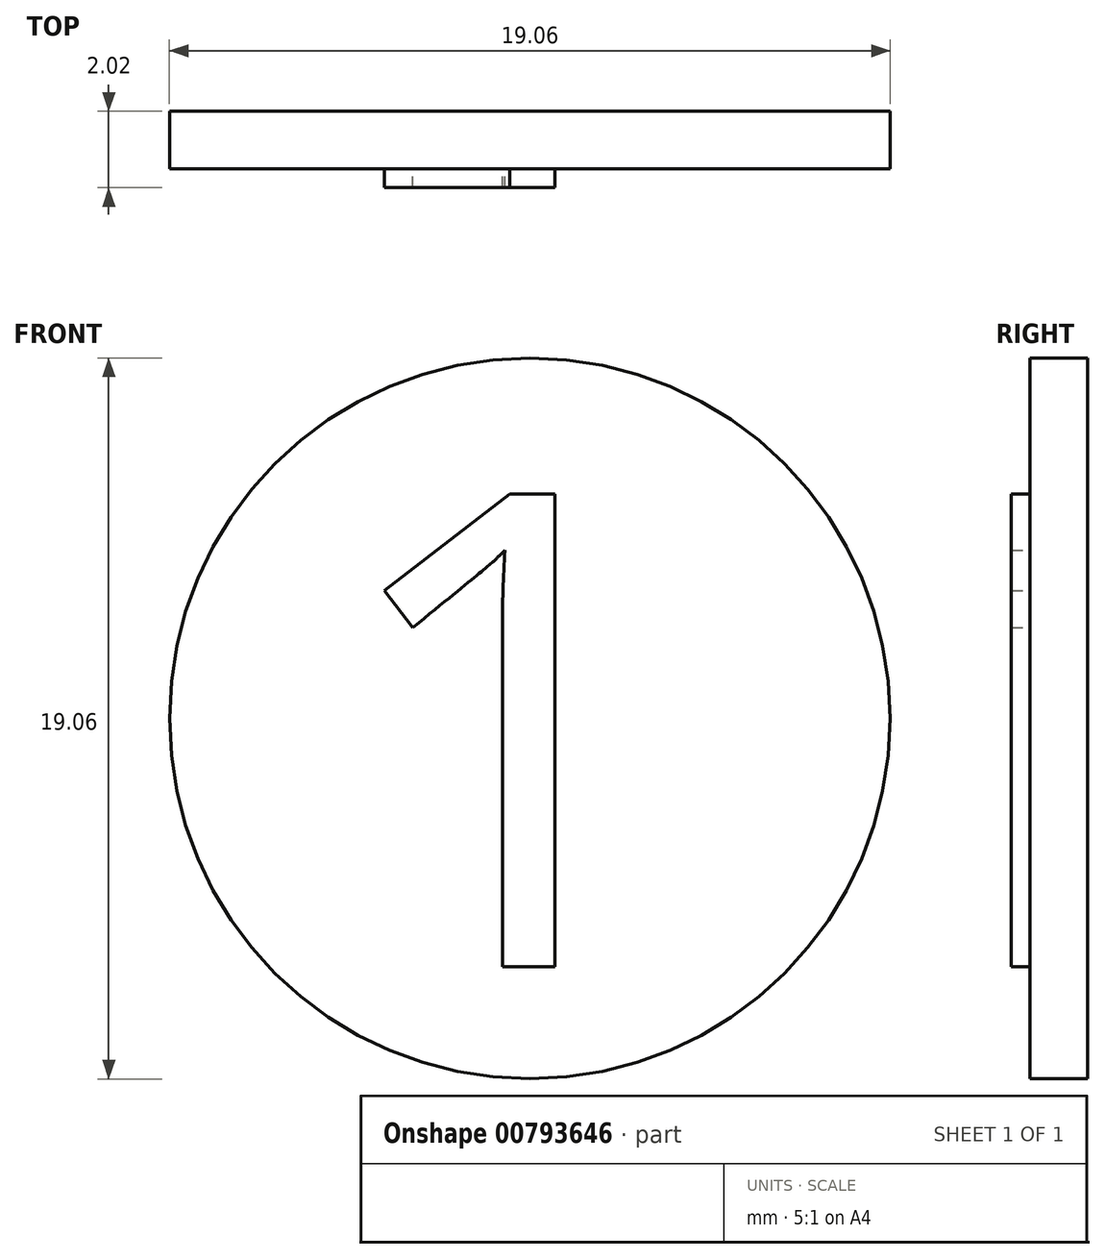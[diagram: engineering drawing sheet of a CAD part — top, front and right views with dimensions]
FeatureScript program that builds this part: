
annotation { "Feature Type Name" : "Feature", "Feature Type Description" : "" }
export const myFeature = defineFeature(function(context is Context, id is Id, definition is map)
    precondition{}
    {
        {
            var Q0;
            Q0=qCreatedBy(makeId("Front.planeOp"),FACE);
            var sketch = newSketch(context, id + "F0", { "sketchPlane" : qUnion([Q0])});
            skCircle(sketch, "E0", {"center": v(0, 0) * mm, "radius": 9.53 * mm});
            skSolve(sketch);
        }
        {
            var Q0;
            Q0=makeQuery(id+"F0.imprint","IMPRINT",FACE,{"disambiguationData":[TD([[makeQuery(id+"F0.imprint","IMPRINT",EDGE,{"derivedFrom":sQuery(id+"F0.wireOp",EDGE,"E0")}),1.0]])]});
            extrude(context, id + "F1", {"entities" : qUnion([Q0]), "depth" : 1.52 * mm, "offsetDistance" : 25 * mm});
        }
        {
            var Q0;
            Q0=makeQuery(id+"F1.opExtrude","CAP_FACE",FACE,{"disambiguationData":[OSD([sQuery(id+"F0.wireOp",EDGE,"E0")])],"isStart":false});
            var sketch = newSketch(context, id + "F2", { "sketchPlane" : qUnion([Q0])});
            skText(sketch, "E1", { "text": "1", "fontName": "OpenSans-Regular.ttf"});
            const initialGuessF2  = {"E1": [-0.00545, -0.00656, 1, 0, 0.0126]};
            skSetInitialGuess(sketch, initialGuessF2);
            skSolve(sketch);
        }
        {
            var Q0;
            Q0=makeQuery(id+"F2.imprint","IMPRINT",FACE,{"disambiguationData":[TD([[makeQuery(id+"F2.imprint","IMPRINT",EDGE,{"derivedFrom":sQuery(id+"F2.wireOp",EDGE,"E1.sketch_text.stroke-0")}),-1.0]])]});
            extrude(context, id + "F3", {"entities" : qUnion([Q0]), "operationType" : NewBodyOperationType.ADD, "depth" : .5 * mm, "offsetDistance" : 25 * mm});
        }
    });
